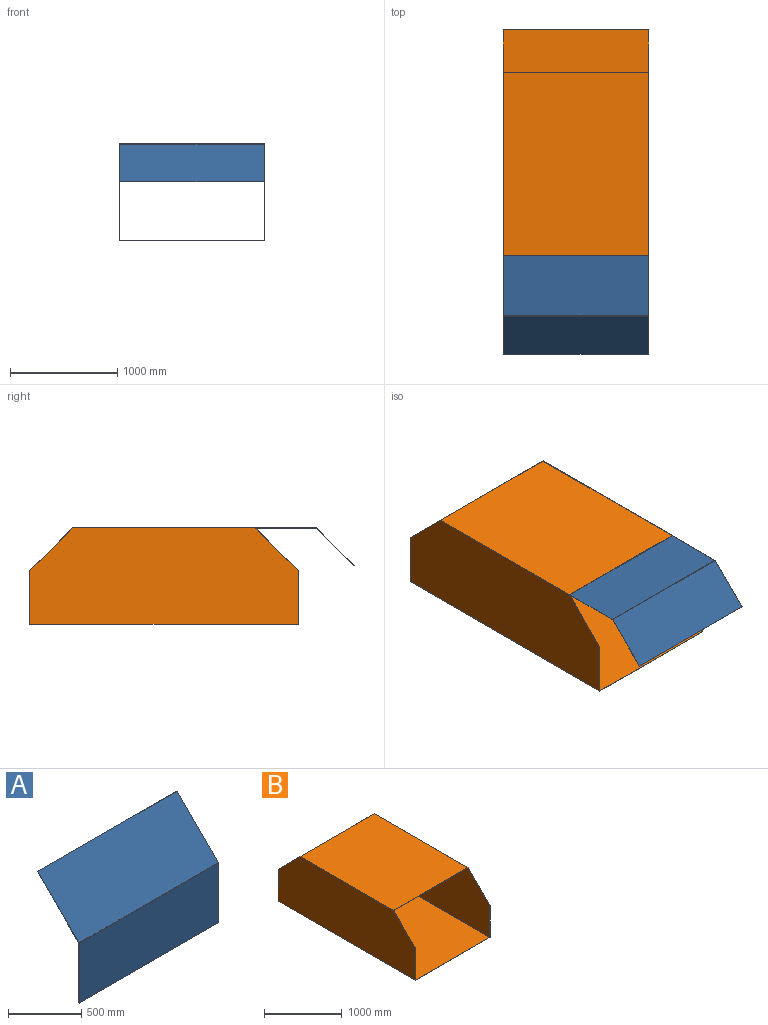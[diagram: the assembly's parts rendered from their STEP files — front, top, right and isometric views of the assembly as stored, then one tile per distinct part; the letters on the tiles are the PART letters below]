
ASSEMBLY  parts=2 mates=1
PART A: 14 faces, bbox 1350x403x902.1 mm
  f0: plane 1350x2.12mm, normal (0,0.71,0.71), area 4050mm2, adj f1,f2,f3,f4
  f1: plane 401.83x401.83mm, normal (-1,0,0), area 1695.8mm2, adj f0,f3,f4,f11
  f2: plane 401.83x401.83mm, normal (1,0,0), area 1695.8mm2, adj f0,f3,f4,f10
  f3: plane 1350x399.71mm, normal (0,-0.71,0.71), area 763116.1mm2, adj f0,f1,f2,f12
  f4: plane 1350x399.71mm, normal (0,0.71,-0.71), area 763116.1mm2, adj f0,f1,f2,f13
  f5: plane 499.59x3mm, normal (-1,0,0), area 1498.8mm2, adj f6,f8,f9,f11
  f6: plane 1350x3mm, normal (0,0,-1), area 4050mm2, adj f5,f7,f8,f9
  f7: plane 499.59x3mm, normal (1,0,0), area 1498.8mm2, adj f6,f8,f9,f10
  f8: plane 1350x499.59mm, normal (0,-1,0), area 674440.8mm2, adj f5,f6,f7,f12
  f9: plane 1350x499.59mm, normal (0,1,0), area 674440.8mm2, adj f5,f6,f7,f13
  f10: plane 3.29x2.83mm, normal (1,0,0), area 5.9mm2, adj f2,f7,f12,f13
  f11: plane 3.29x2.83mm, normal (-1,0,0), area 5.9mm2, adj f1,f5,f12,f13
  f12: cylinder r=4mm len=1350mm, axis (1,0,0), area 4241.2mm2, adj f3,f8,f10,f11
  f13: cylinder r=1mm len=1350mm, axis (1,0,0), area 1060.3mm2, adj f4,f9,f10,f11
PART B: 12 faces, bbox 1355x2500x900 mm
  f0: plane 1355x500mm, normal (0,1,0), area 5875mm2, adj f1,f5,f6,f7,f9,f10,f11
  f1: plane 1355x400mm, normal (0,0.71,0.71), area 7601.4mm2, adj f0,f3,f6,f7,f8,f10,f11
  f2: plane 1355x400mm, normal (0,-0.71,0.71), area 7601.4mm2, adj f3,f4,f6,f7,f8,f10,f11
  f3: plane 1700x1355mm, normal (0,0,1), area 2303500mm2, adj f1,f2,f6,f7
  f4: plane 1355x500mm, normal (0,-1,0), area 5875mm2, adj f2,f5,f6,f7,f9,f10,f11
  f5: plane 2500x1355mm, normal (0,0,-1), area 3387500mm2, adj f0,f4,f6,f7
  f6: plane 2500x900mm, normal (1,0,0), area 2090000mm2, adj f0,f1,f2,f3,f4,f5
  f7: plane 2500x900mm, normal (-1,0,0), area 2090000mm2, adj f0,f1,f2,f3,f4,f5
  f8: plane 1705x1350mm, normal (0,0,-1), area 2301750mm2, adj f1,f2,f10,f11
  f9: plane 2500x1350mm, normal (0,0,1), area 3375000mm2, adj f0,f4,f10,f11
  f10: plane 2500x895mm, normal (-1,0,0), area 2079493.8mm2, adj f0,f1,f2,f4,f8,f9
  f11: plane 2500x895mm, normal (1,0,0), area 2079493.7mm2, adj f0,f1,f2,f4,f8,f9
PLACE A rot(axis=(-1,0,0),45deg) t=(-341.41,375.93,-899.28)mm
PLACE B t=(-341.16,1261.29,-558.85)mm
MATE planar A.f3 <-> B.f3  axis (0,0,1) through (-341.41,411.29,341.15)mm
